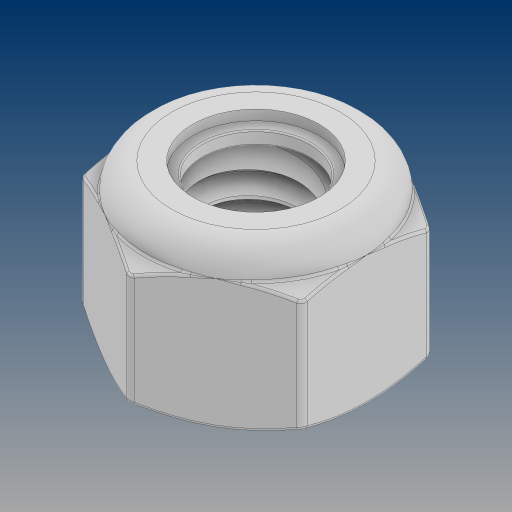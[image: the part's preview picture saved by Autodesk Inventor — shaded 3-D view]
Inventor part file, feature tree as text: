
AUTODESK INVENTOR PART (.ipt)
format: ipt  version: 2024.3 (Build 283343000, 343)  size: 651,776 bytes
history: native  units: in
note: dims shown in document units (in); Inventor stores cm internally (conversion verified against a paired STEP export)
features: fillet x1, boolean_combine x1
ambient origin geometry x8: Origin, YZ Plane, XZ Plane, XY Plane, X Axis, Y Axis, Z Axis, Center Point
bodies: Solid1 (feature_tree), Solid2 (feature_tree)
feature tree (2):
  fillet  "Fillet1"  [1 undecoded]
  boolean_combine  "Combine1"
note: 1 required parameter value undecoded (feature->parameter linkage not recoverable at this tier; creation-order binding heuristic only, values carry confidence <= 0.55)
